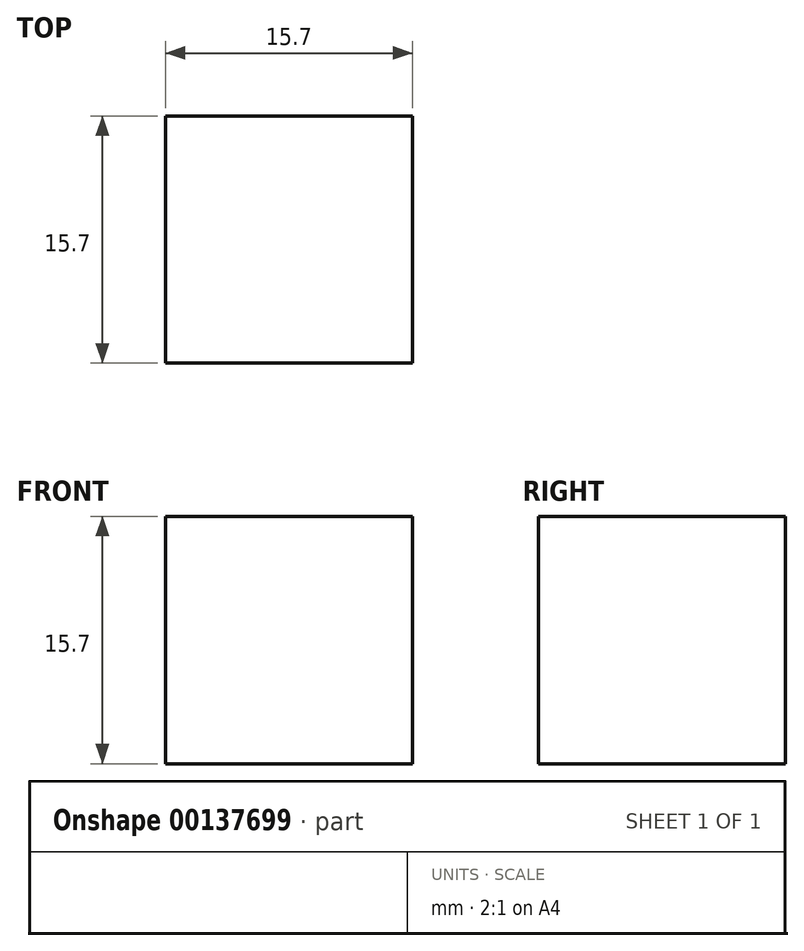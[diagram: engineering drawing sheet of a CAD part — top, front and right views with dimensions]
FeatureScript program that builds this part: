
annotation { "Feature Type Name" : "Feature", "Feature Type Description" : "" }
export const myFeature = defineFeature(function(context is Context, id is Id, definition is map)
    precondition{}
    {
        {
            var Q0;
            Q0=qCreatedBy(makeId("Front.planeOp"),FACE);
            var sketch = newSketch(context, id + "F0", { "sketchPlane" : qUnion([Q0])});
            skLineSegment(sketch, "E0.bottom", {"start": v(8.47, -37.64) * mm, "end": v(-7.23, -37.64) * mm});
            skLineSegment(sketch, "E0.top", {"start": v(8.47, -21.94) * mm, "end": v(-7.23, -21.94) * mm});
            skLineSegment(sketch, "E0.left", {"start": v(8.47, -37.64) * mm, "end": v(8.47, -21.94) * mm});
            skLineSegment(sketch, "E0.right", {"start": v(-7.23, -37.64) * mm, "end": v(-7.23, -21.94) * mm});
            skLineSegment(sketch, "E1.bottom", {"start": v(-7.23, -21.94) * mm, "end": v(8.47, -21.94) * mm});
            skLineSegment(sketch, "E1.top", {"start": v(-7.23, -6.25) * mm, "end": v(8.47, -6.25) * mm});
            skLineSegment(sketch, "E1.left", {"start": v(-7.23, -21.94) * mm, "end": v(-7.23, -6.25) * mm});
            skLineSegment(sketch, "E1.right", {"start": v(8.47, -21.94) * mm, "end": v(8.47, -6.25) * mm});
            skSolve(sketch);
        }
        {
            var Q0;
            Q0=makeQuery(id+"F0.imprint","IMPRINT",FACE,{"disambiguationData":[TD([[makeQuery(id+"F0.imprint","IMPRINT",EDGE,{"derivedFrom":sQuery(id+"F0.wireOp",EDGE,"E0.bottom")}),-1.0]])]});
            extrude(context, id + "F1", {"entities" : qUnion([Q0]), "depth" : 7.85 * mm});
        }
        {
            var Q0;
            Q0=makeQuery(id+"F0.imprint","IMPRINT",FACE,{"disambiguationData":[TD([[makeQuery(id+"F0.imprint","IMPRINT",EDGE,{"derivedFrom":sQuery(id+"F0.wireOp",EDGE,"E1.bottom")}),1.0]])]});
            var Q1;
            Q1=makeQuery(id+"F0.imprint","IMPRINT",FACE,{"disambiguationData":[TD([[makeQuery(id+"F0.imprint","IMPRINT",EDGE,{"derivedFrom":sQuery(id+"F0.wireOp",EDGE,"E0.bottom")}),-1.0]])]});
            extrude(context, id + "F2", {"entities" : qUnion([Q0, Q1]), "operationType" : NewBodyOperationType.ADD, "oppositeDirection" : true, "depth" : 7.85 * mm});
        }
    });
